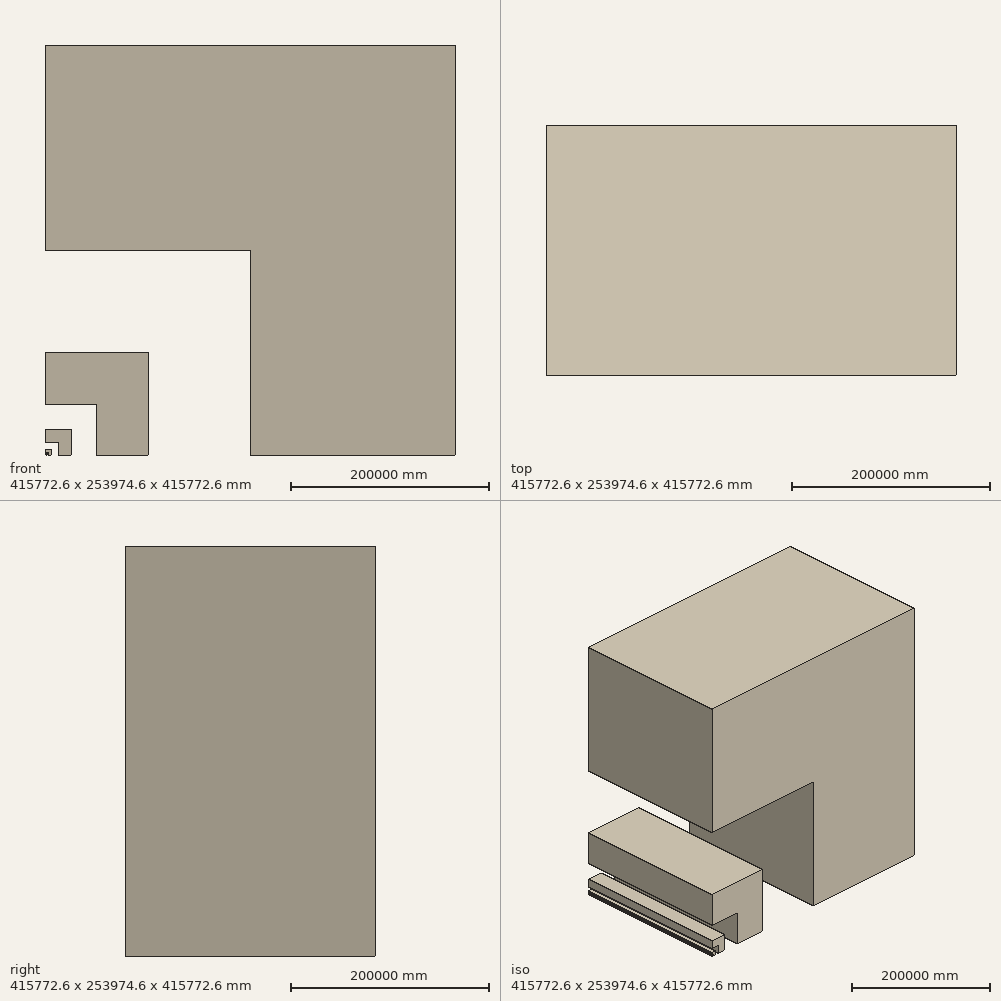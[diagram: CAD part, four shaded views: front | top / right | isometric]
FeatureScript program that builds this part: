
annotation { "Feature Type Name" : "Feature", "Feature Type Description" : "" }
export const myFeature = defineFeature(function(context is Context, id is Id, definition is map)
    precondition{}
    {
        {
            var Q0;
            Q0=qCreatedBy(makeId("Front.planeOp"),FACE);
            var sketch = newSketch(context, id + "F0", { "sketchPlane" : qUnion([Q0])});
            skLineSegment(sketch, "E0", {"start": v(0, 0) * mm, "end": v(-25.4, 0) * mm});
            skLineSegment(sketch, "E1", {"start": v(-25.4, 0) * mm, "end": v(-25.4, -25.4) * mm});
            skLineSegment(sketch, "E2", {"start": v(-25.4, -25.4) * mm, "end": v(0, -25.4) * mm});
            skLineSegment(sketch, "E3", {"start": v(0, 0) * mm, "end": v(0, -25.4) * mm});
            skLineSegment(sketch, "E4", {"start": v(-25.4, 0) * mm, "end": v(-25.4, 25.4) * mm});
            skLineSegment(sketch, "E5", {"start": v(0, -25.4) * mm, "end": v(25.4, -25.4) * mm});
            skLineSegment(sketch, "E6", {"start": v(25.4, -25.4) * mm, "end": v(25.4, 25.4) * mm});
            skLineSegment(sketch, "E7", {"start": v(25.4, 25.4) * mm, "end": v(-25.4, 25.4) * mm});
            skLineSegment(sketch, "E8", {"start": v(-25.4, 76.2) * mm, "end": v(-25.4, 25.4) * mm});
            skLineSegment(sketch, "E9", {"start": v(25.4, -25.4) * mm, "end": v(76.2, -25.4) * mm});
            skLineSegment(sketch, "E10", {"start": v(76.2, -25.4) * mm, "end": v(76.2, 76.2) * mm});
            skLineSegment(sketch, "E11", {"start": v(76.2, 76.2) * mm, "end": v(-25.4, 76.2) * mm});
            skLineSegment(sketch, "E12", {"start": v(-25.4, 76.2) * mm, "end": v(-25.4, 177.8) * mm});
            skLineSegment(sketch, "E13", {"start": v(76.2, -25.4) * mm, "end": v(177.8, -25.4) * mm});
            skLineSegment(sketch, "E14", {"start": v(177.8, -25.4) * mm, "end": v(177.8, 177.8) * mm});
            skLineSegment(sketch, "E15", {"start": v(177.8, 177.8) * mm, "end": v(-25.4, 177.8) * mm});
            skLineSegment(sketch, "E16", {"start": v(-25.4, 381) * mm, "end": v(-25.4, 177.8) * mm});
            skLineSegment(sketch, "E17", {"start": v(-25.4, 381) * mm, "end": v(381, 381) * mm});
            skLineSegment(sketch, "E18", {"start": v(381, 381) * mm, "end": v(381, -25.4) * mm});
            skLineSegment(sketch, "E19", {"start": v(381, -25.4) * mm, "end": v(177.8, -25.4) * mm});
            skLineSegment(sketch, "E20", {"start": v(-25.4, 381) * mm, "end": v(-25.4, 787.4) * mm});
            skLineSegment(sketch, "E21", {"start": v(-25.4, 787.4) * mm, "end": v(787.4, 787.4) * mm});
            skLineSegment(sketch, "E22", {"start": v(787.4, 787.4) * mm, "end": v(787.4, -25.4) * mm});
            skLineSegment(sketch, "E23", {"start": v(787.4, -25.4) * mm, "end": v(381, -25.4) * mm});
            skLineSegment(sketch, "E24", {"start": v(-25.4, 787.4) * mm, "end": v(-25.4, 1600.2) * mm});
            skLineSegment(sketch, "E25", {"start": v(-25.4, 1600.2) * mm, "end": v(1600.2, 1600.2) * mm});
            skLineSegment(sketch, "E26", {"start": v(1600.2, 1600.2) * mm, "end": v(1600.2, -25.4) * mm});
            skLineSegment(sketch, "E27", {"start": v(1600.2, -25.4) * mm, "end": v(787.4, -25.4) * mm});
            skLineSegment(sketch, "E28", {"start": v(-25.4, 1600.2) * mm, "end": v(-25.4, 3225.8) * mm});
            skLineSegment(sketch, "E29", {"start": v(-25.4, 3225.8) * mm, "end": v(3225.8, 3225.8) * mm});
            skLineSegment(sketch, "E30", {"start": v(3225.8, 3225.8) * mm, "end": v(3225.8, -25.4) * mm});
            skLineSegment(sketch, "E31", {"start": v(3225.8, -25.4) * mm, "end": v(1600.2, -25.4) * mm});
            skLineSegment(sketch, "E32", {"start": v(-25.4, 3225.8) * mm, "end": v(-25.4, 6477) * mm});
            skLineSegment(sketch, "E33", {"start": v(3225.8, -25.4) * mm, "end": v(6477, -25.4) * mm});
            skLineSegment(sketch, "E34", {"start": v(6477, -25.4) * mm, "end": v(6477, 6477) * mm});
            skLineSegment(sketch, "E35", {"start": v(6477, 6477) * mm, "end": v(-25.4, 6477) * mm});
            skLineSegment(sketch, "E36", {"start": v(-25.4, 6477) * mm, "end": v(-25.4, 12979.4) * mm});
            skLineSegment(sketch, "E37", {"start": v(6477, -25.4) * mm, "end": v(12979.4, -25.4) * mm});
            skLineSegment(sketch, "E38", {"start": v(12979.4, -25.4) * mm, "end": v(12979.4, 12979.4) * mm});
            skLineSegment(sketch, "E39", {"start": v(12979.4, 12979.4) * mm, "end": v(-25.4, 12979.4) * mm});
            skLineSegment(sketch, "E40", {"start": v(-25.4, 12979.4) * mm, "end": v(0, 25984.18) * mm});
            skLineSegment(sketch, "E41", {"start": v(12979.4, -25.4) * mm, "end": v(25984.2, -25.4) * mm});
            skLineSegment(sketch, "E42", {"start": v(25984.2, -25.4) * mm, "end": v(25984.2, 25984.18) * mm});
            skLineSegment(sketch, "E43", {"start": v(25984.2, 25984.18) * mm, "end": v(0, 25984.18) * mm});
            skLineSegment(sketch, "E44", {"start": v(0, 25984.18) * mm, "end": v(0, 51968.38) * mm});
            skLineSegment(sketch, "E45", {"start": v(25984.2, -25.4) * mm, "end": v(51968.4, -25.4) * mm});
            skLineSegment(sketch, "E46", {"start": v(51968.4, -25.4) * mm, "end": v(51968.4, 51968.38) * mm});
            skLineSegment(sketch, "E47", {"start": v(51968.4, 51968.38) * mm, "end": v(0, 51968.38) * mm});
            skLineSegment(sketch, "E48", {"start": v(0, 51968.38) * mm, "end": v(0, 103936.78) * mm});
            skLineSegment(sketch, "E49", {"start": v(51968.4, -25.4) * mm, "end": v(103936.8, -25.4) * mm});
            skLineSegment(sketch, "E50", {"start": v(103936.8, -25.4) * mm, "end": v(103936.8, 103936.78) * mm});
            skLineSegment(sketch, "E51", {"start": v(103936.8, 103936.78) * mm, "end": v(0, 103936.78) * mm});
            skLineSegment(sketch, "E52", {"start": v(0, 103936.78) * mm, "end": v(0, 207873.58) * mm});
            skLineSegment(sketch, "E53", {"start": v(103936.8, -25.4) * mm, "end": v(207873.6, -25.4) * mm});
            skLineSegment(sketch, "E54", {"start": v(207873.6, -25.4) * mm, "end": v(207873.6, 207873.58) * mm});
            skLineSegment(sketch, "E55", {"start": v(207873.6, 207873.58) * mm, "end": v(0, 207873.58) * mm});
            skLineSegment(sketch, "E56", {"start": v(0, 207873.58) * mm, "end": v(0, 415747.18) * mm});
            skLineSegment(sketch, "E57", {"start": v(207873.6, -25.4) * mm, "end": v(415747.2, -25.4) * mm});
            skLineSegment(sketch, "E58", {"start": v(415747.2, -25.4) * mm, "end": v(415747.2, 415747.18) * mm});
            skLineSegment(sketch, "E59", {"start": v(415747.2, 415747.18) * mm, "end": v(0, 415747.18) * mm});
            skSolve(sketch);
        }
        {
            var Q0;
            Q0=makeQuery(id+"F0.imprint","IMPRINT",FACE,{"disambiguationData":[TD([[makeQuery(id+"F0.imprint","IMPRINT",EDGE,{"derivedFrom":sQuery(id+"F0.wireOp",EDGE,"E0")}),1.0]])]});
            var Q1;
            Q1=makeQuery(id+"F0.imprint","IMPRINT",FACE,{"disambiguationData":[TD([[makeQuery(id+"F0.imprint","IMPRINT",EDGE,{"derivedFrom":sQuery(id+"F0.wireOp",EDGE,"E6")}),-1.0]])]});
            var Q2;
            Q2=makeQuery(id+"F0.imprint","IMPRINT",FACE,{"disambiguationData":[TD([[makeQuery(id+"F0.imprint","IMPRINT",EDGE,{"derivedFrom":sQuery(id+"F0.wireOp",EDGE,"E14")}),-1.0]])]});
            var Q3;
            Q3=makeQuery(id+"F0.imprint","IMPRINT",FACE,{"disambiguationData":[TD([[makeQuery(id+"F0.imprint","IMPRINT",EDGE,{"derivedFrom":sQuery(id+"F0.wireOp",EDGE,"E21")}),1.0]])]});
            var Q4;
            Q4=makeQuery(id+"F0.imprint","IMPRINT",FACE,{"disambiguationData":[TD([[makeQuery(id+"F0.imprint","IMPRINT",EDGE,{"derivedFrom":sQuery(id+"F0.wireOp",EDGE,"E29")}),1.0]])]});
            var Q5;
            Q5=makeQuery(id+"F0.imprint","IMPRINT",FACE,{"disambiguationData":[TD([[makeQuery(id+"F0.imprint","IMPRINT",EDGE,{"derivedFrom":sQuery(id+"F0.wireOp",EDGE,"E38")}),-1.0]])]});
            var Q6;
            Q6=makeQuery(id+"F0.imprint","IMPRINT",FACE,{"disambiguationData":[TD([[makeQuery(id+"F0.imprint","IMPRINT",EDGE,{"derivedFrom":sQuery(id+"F0.wireOp",EDGE,"E46")}),-1.0]])]});
            var Q7;
            Q7=makeQuery(id+"F0.imprint","IMPRINT",FACE,{"disambiguationData":[TD([[makeQuery(id+"F0.imprint","IMPRINT",EDGE,{"derivedFrom":sQuery(id+"F0.wireOp",EDGE,"E54")}),-1.0]])]});
            extrude(context, id + "F1", {"entities" : qUnion([Q0, Q1, Q2, Q3, Q4, Q5, Q6, Q7]), "depth" : 253974.6 * mm});
        }
    });
